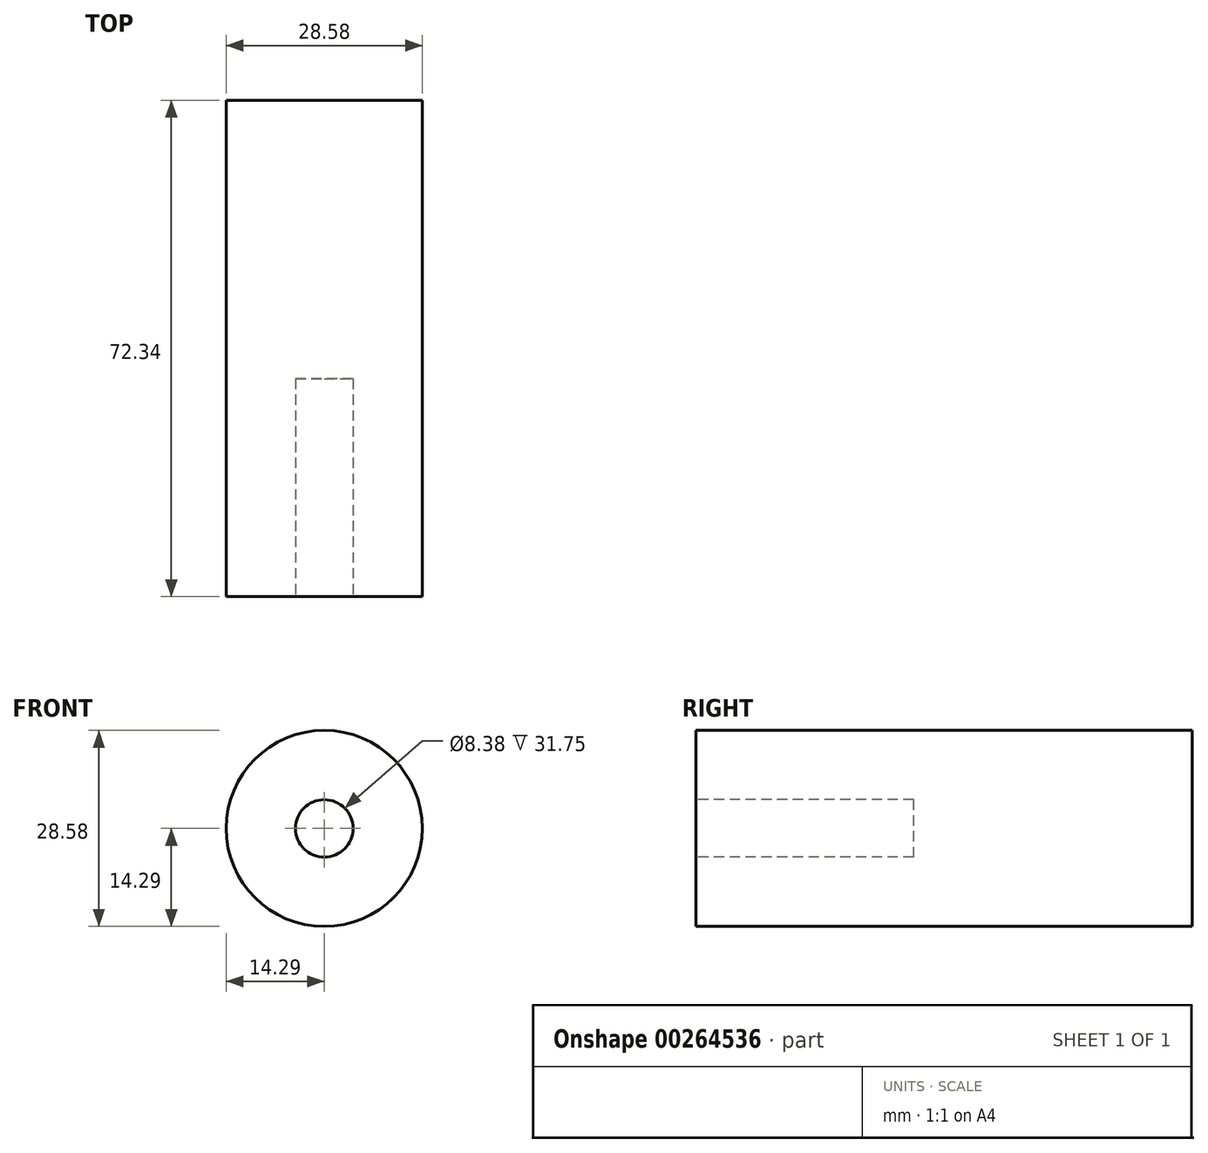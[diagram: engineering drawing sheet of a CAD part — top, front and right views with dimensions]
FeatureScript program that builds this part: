
annotation { "Feature Type Name" : "Feature", "Feature Type Description" : "" }
export const myFeature = defineFeature(function(context is Context, id is Id, definition is map)
    precondition{}
    {
        {
            var Q0;
            Q0=qCreatedBy(makeId("Front.planeOp"),FACE);
            var sketch = newSketch(context, id + "F3", { "sketchPlane" : qUnion([Q0])});
            skCircle(sketch, "E0", {"center": v(0, 0) * mm, "radius": 14.29 * mm});
            skSolve(sketch);
        }
        {
            var Q0;
            Q0=qSketchRegion(id+"F3",true);
            extrude(context, id + "F0", {"entities" : qUnion([Q0]), "depth" : 66.5 * mm + 5.85 * mm, "symmetric" : true});
        }
        {
            var Q0;
            Q0=makeQuery(id+"F0.opExtrude","CAP_FACE",FACE,{"disambiguationData":[OSD([sQuery(id+"F3.wireOp",EDGE,"E0")])],"isStart":false});
            var sketch = newSketch(context, id + "F1", { "sketchPlane" : qUnion([Q0])});
            skCircle(sketch, "E1", {"center": v(0, 0) * mm, "radius": 4.2 * mm});
            skSolve(sketch);
        }
        {
            var Q0;
            Q0=qSketchRegion(id+"F1",true);
            extrude(context, id + "F2", {"entities" : qUnion([Q0]), "operationType" : NewBodyOperationType.REMOVE, "oppositeDirection" : true, "depth" : 31.75 * mm});
        }
    });
